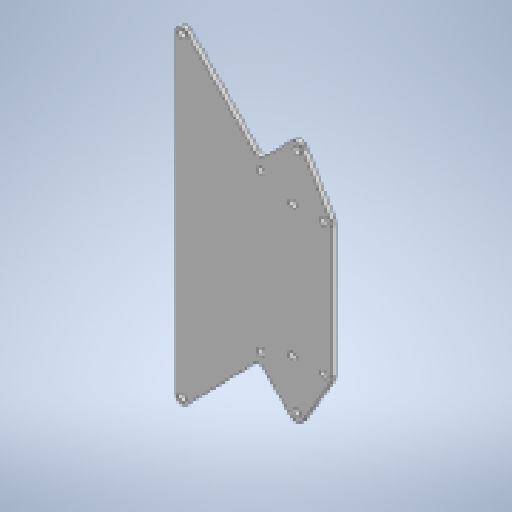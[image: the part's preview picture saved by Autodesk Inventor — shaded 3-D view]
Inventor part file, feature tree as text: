
AUTODESK INVENTOR PART (.ipt)
format: ipt  version: 2025.1 (Build 291241000, 241)  size: 289,792 bytes
history: native  units: mm
features: reference x13, other x6, extrude x4, fillet x4, sketch x4
ambient origin geometry x8: Origin, YZ Plane, XZ Plane, XY Plane, X Axis, Y Axis, Z Axis, Center Point
bodies: Body1 (feature_tree)
feature tree (31):
  other  "ソリッド1"
  extrude  "押し出し1"  Depth=2.2mm
  fillet  "フィレット1"  Radius=4.0mm
  extrude  "押し出し2"  Depth=1.5mm TaperAngle=0.0deg
  fillet  "フィレット2"  Radius=2.0mm
  extrude  "押し出し3"  Depth=1.0mm
  fillet  "フィレット3"  Radius=2.0mm
  extrude  "押し出し4"  Depth=2.0mm
  fillet  "フィレット4"  Radius=1.0mm
  sketch  "スケッチ1"
  reference  "参照1"
  reference  "参照2"
  reference  "参照3"
  sketch  "スケッチ2"
  reference  "参照4"
  reference  "参照5"
  reference  "参照6"
  reference  "参照7"
  reference  "参照8"
  reference  "参照9"
  reference  "参照10"
  reference  "参照11"
  reference  "参照12"
  sketch  "スケッチ3"
  reference  "参照13"
  sketch  "スケッチ4"
  other  "Assembly1"
  other  "piti_mata:3"
  other  "piti_mata:1"
  other  "KRS2500_scale:1"
  other  "KRS2500_scale:2"
